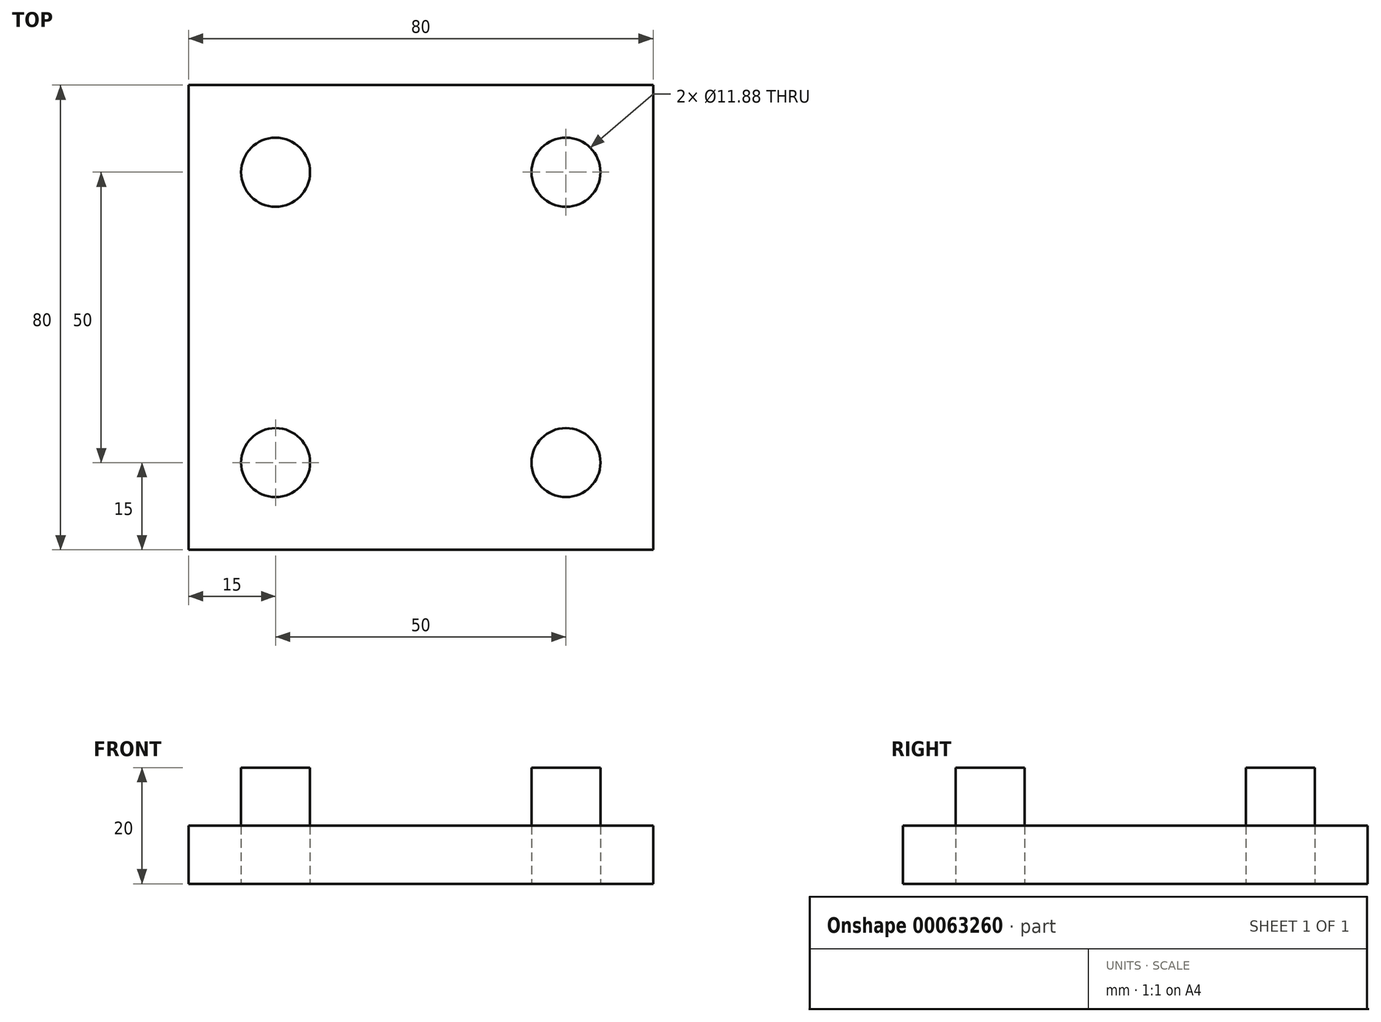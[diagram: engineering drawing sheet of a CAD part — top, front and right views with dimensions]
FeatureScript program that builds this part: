
annotation { "Feature Type Name" : "Feature", "Feature Type Description" : "" }
export const myFeature = defineFeature(function(context is Context, id is Id, definition is map)
    precondition{}
    {
        {
            var Q0;
            Q0=qCreatedBy(makeId("Top.planeOp"),FACE);
            var sketch = newSketch(context, id + "F0", { "sketchPlane" : qUnion([Q0])});
            skLineSegment(sketch, "E0.rect.bottom", {"start": v(40, 40) * mm, "end": v(-40, 40) * mm});
            skLineSegment(sketch, "E0.rect.top", {"start": v(40, -40) * mm, "end": v(-40, -40) * mm});
            skLineSegment(sketch, "E0.rect.left", {"start": v(40, 40) * mm, "end": v(40, -40) * mm});
            skLineSegment(sketch, "E0.rect.right", {"start": v(-40, 40) * mm, "end": v(-40, -40) * mm});
            skPoint(sketch, "E0.rect.middle", {"position": v(0, 0) * mm});
            skCircle(sketch, "E1", {"center": v(-25, 25) * mm, "radius": 5.94 * mm});
            skCircle(sketch, "E2.1.1", {"center": v(-25, -25) * mm, "radius": 5.94 * mm});
            skCircle(sketch, "E2.2.1", {"center": v(25, -25) * mm, "radius": 5.94 * mm});
            skCircle(sketch, "E3.1.3.0", {"center": v(25, 25) * mm, "radius": 5.94 * mm});
            skSolve(sketch);
        }
        {
            var Q0;
            Q0=makeQuery(id+"F0.imprint","IMPRINT",FACE,{"disambiguationData":[TD([[makeQuery(id+"F0.imprint","IMPRINT",EDGE,{"derivedFrom":sQuery(id+"F0.wireOp",EDGE,"E0.rect.bottom")}),1.0]])]});
            extrude(context, id + "F1", {"entities" : qUnion([Q0]), "depth" : 10 * mm});
        }
        {
            var Q0;
            Q0=makeQuery(id+"F0.imprint","IMPRINT",FACE,{"disambiguationData":[TD([[makeQuery(id+"F0.imprint","IMPRINT",EDGE,{"derivedFrom":sQuery(id+"F0.wireOp",EDGE,"E1")}),1.0]])]});
            var Q1;
            Q1=makeQuery(id+"F0.imprint","IMPRINT",FACE,{"disambiguationData":[TD([[makeQuery(id+"F0.imprint","IMPRINT",EDGE,{"derivedFrom":sQuery(id+"F0.wireOp",EDGE,"E2.2.1")}),1.0]])]});
            extrude(context, id + "F2", {"entities" : qUnion([Q0, Q1]), "operationType" : NewBodyOperationType.ADD, "depth" : 20 * mm});
        }
    });
